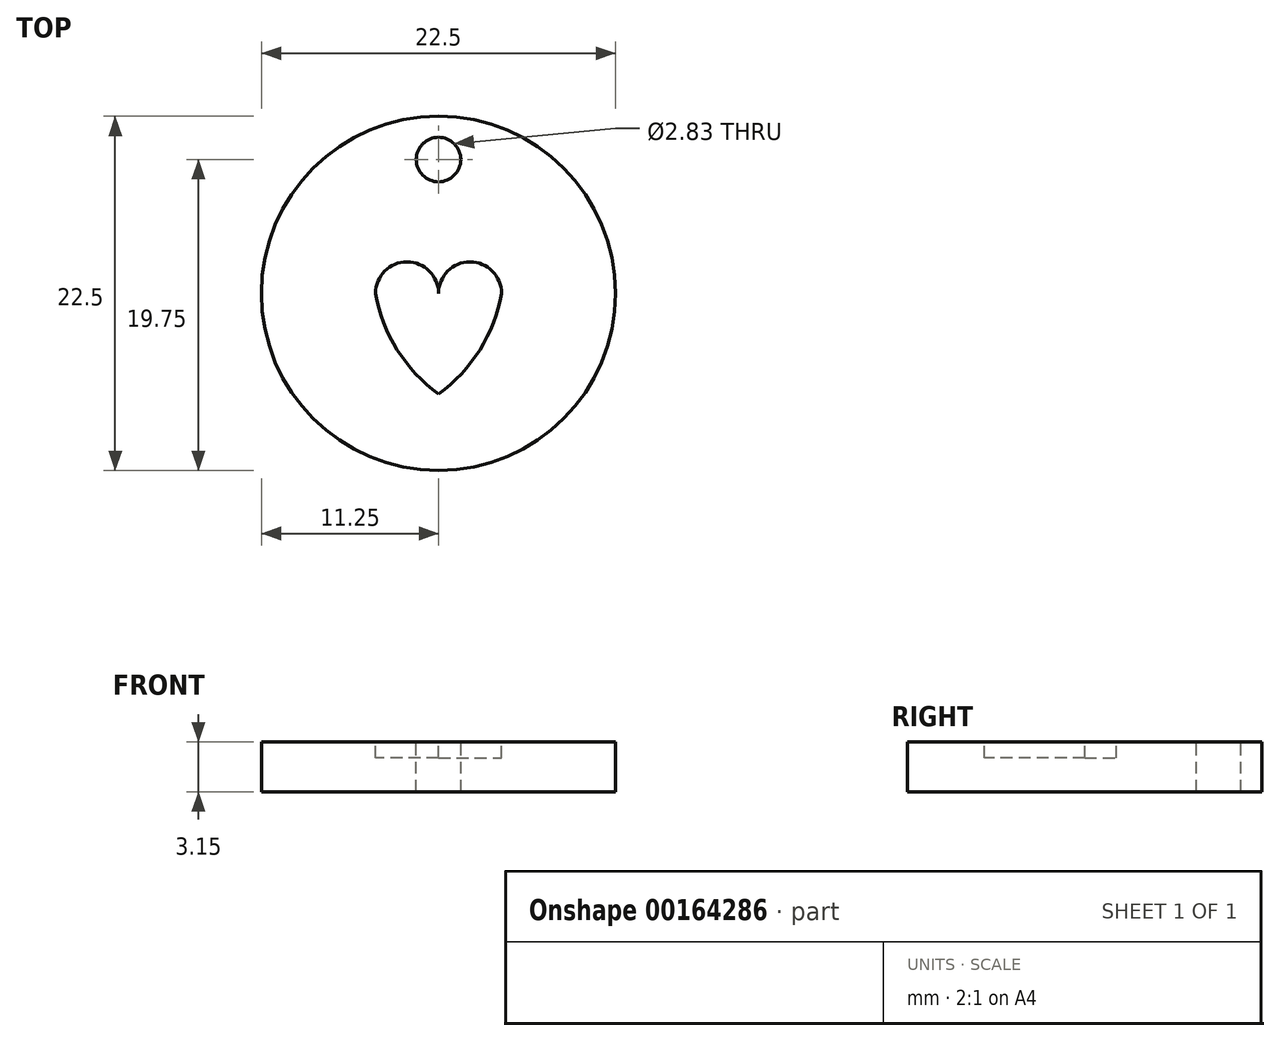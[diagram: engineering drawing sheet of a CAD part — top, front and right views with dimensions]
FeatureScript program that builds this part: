
annotation { "Feature Type Name" : "Feature", "Feature Type Description" : "" }
export const myFeature = defineFeature(function(context is Context, id is Id, definition is map)
    precondition{}
    {
        {
            var Q0;
            Q0=qCreatedBy(makeId("Top.planeOp"),FACE);
            var sketch = newSketch(context, id + "F2", { "sketchPlane" : qUnion([Q0])});
            skCircle(sketch, "E0", {"center": v(0, 0) * mm, "radius": 11.25 * mm});
            skSolve(sketch);
        }
        {
            var Q0;
            Q0=makeQuery(id+"F2.imprint","IMPRINT",FACE,{"disambiguationData":[TD([[makeQuery(id+"F2.imprint","IMPRINT",EDGE,{"derivedFrom":sQuery(id+"F2.wireOp",EDGE,"E0")}),1.0]])]});
            var Q1;
            Q1=sQuery(id+"F2.wireOp",EDGE,"E0");
            extrude(context, id + "F0", {"entities" : qUnion([Q0]), "surfaceEntities" : qUnion([Q1]), "depth" : 3.15 * mm});
        }
        {
            var Q0;
            Q0=makeQuery(id+"F0.opExtrude","CAP_FACE",FACE,{"disambiguationData":[OSD([sQuery(id+"F2.wireOp",EDGE,"E0")])],"isStart":false});
            var sketch = newSketch(context, id + "F3", { "sketchPlane" : qUnion([Q0])});
            skCircle(sketch, "E1", {"center": v(0, 8.5) * mm, "radius": 1.5 * mm});
            skCircle(sketch, "E2", {"center": v(0, 8.5) * mm, "radius": 1.41 * mm});
            skSolve(sketch);
        }
        {
            var Q0;
            Q0=makeQuery(id+"F3.imprint","IMPRINT",FACE,{"disambiguationData":[TD([[makeQuery(id+"F3.imprint","IMPRINT",EDGE,{"derivedFrom":sQuery(id+"F3.wireOp",EDGE,"E2")}),1.0]])]});
            extrude(context, id + "F4", {"entities" : qUnion([Q0]), "operationType" : NewBodyOperationType.REMOVE, "endBound" : BoundingType.UP_TO_NEXT, "oppositeDirection" : true, "depth" : 25 * mm});
        }
        {
            var Q0;
            Q0=makeQuery(id+"F0.opExtrude","CAP_FACE",FACE,{"disambiguationData":[OSD([sQuery(id+"F2.wireOp",EDGE,"E0")])],"isStart":false});
            var sketch = newSketch(context, id + "F1", { "sketchPlane" : qUnion([Q0])});
            skPoint(sketch, "E3", {"position": v(0, -6.4) * mm});
            skPoint(sketch, "E4", {"position": v(4, 0) * mm});
            skPoint(sketch, "E5", {"position": v(0, 0) * mm});
            skPoint(sketch, "E6", {"position": v(-4, 0) * mm});
            skArc(sketch, "E7", {"start": v(-4, 0) * mm, "mid": v(-2.63, -3.59) * mm, "end": v(0, -6.4) * mm});
            skArc(sketch, "E8", {"start": v(0, -6.4) * mm, "mid": v(2.63, -3.59) * mm, "end": v(4, 0) * mm});
            skArc(sketch, "E9", {"start": v(0, 0) * mm, "mid": v(-2, 2) * mm, "end": v(-4, 0) * mm});
            skArc(sketch, "E10", {"start": v(4, 0) * mm, "mid": v(2, 2) * mm, "end": v(0, 0) * mm});
            skSolve(sketch);
        }
        {
            var Q0;
            Q0=makeQuery(id+"F1.imprint","IMPRINT",FACE,{"disambiguationData":[TD([[makeQuery(id+"F1.imprint","IMPRINT",EDGE,{"derivedFrom":sQuery(id+"F1.wireOp",EDGE,"E7")}),1.0]])]});
            extrude(context, id + "F5", {"entities" : qUnion([Q0]), "operationType" : NewBodyOperationType.REMOVE, "oppositeDirection" : true, "depth" : 1 * mm});
        }
    });
